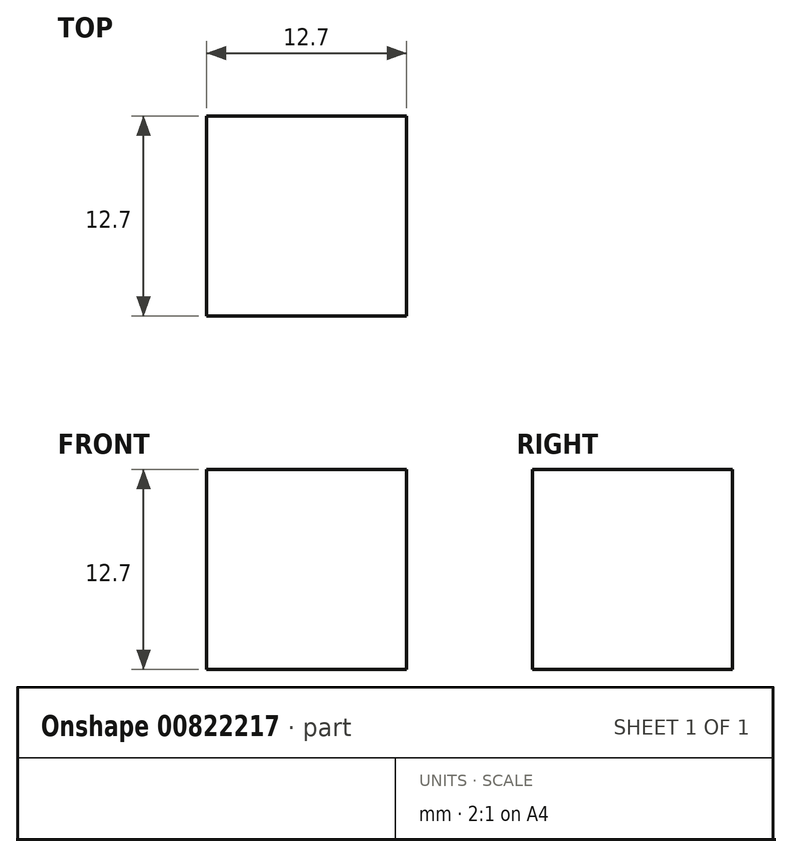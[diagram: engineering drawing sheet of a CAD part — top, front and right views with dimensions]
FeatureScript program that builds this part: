
annotation { "Feature Type Name" : "Feature", "Feature Type Description" : "" }
export const myFeature = defineFeature(function(context is Context, id is Id, definition is map)
    precondition{}
    {
        {
            var Q0;
            Q0=qCreatedBy(makeId("Front.planeOp"),FACE);
            var sketch = newSketch(context, id + "F0", { "sketchPlane" : qUnion([Q0])});
            skLineSegment(sketch, "E0.bottom", {"start": v(0, 0) * mm, "end": v(12.7, 0) * mm});
            skLineSegment(sketch, "E0.top", {"start": v(0, 12.7) * mm, "end": v(12.7, 12.7) * mm});
            skLineSegment(sketch, "E0.left", {"start": v(0, 0) * mm, "end": v(0, 12.7) * mm});
            skLineSegment(sketch, "E0.right", {"start": v(12.7, 0) * mm, "end": v(12.7, 12.7) * mm});
            skSolve(sketch);
        }
        {
            var Q0;
            Q0 = qSketchRegion(id + "F0", true);
            extrude(context, id + "F1", {"entities" : qUnion([Q0]), "depth" : 12.7 * mm, "offsetDistance" : 25.4 * mm});
        }
    });
